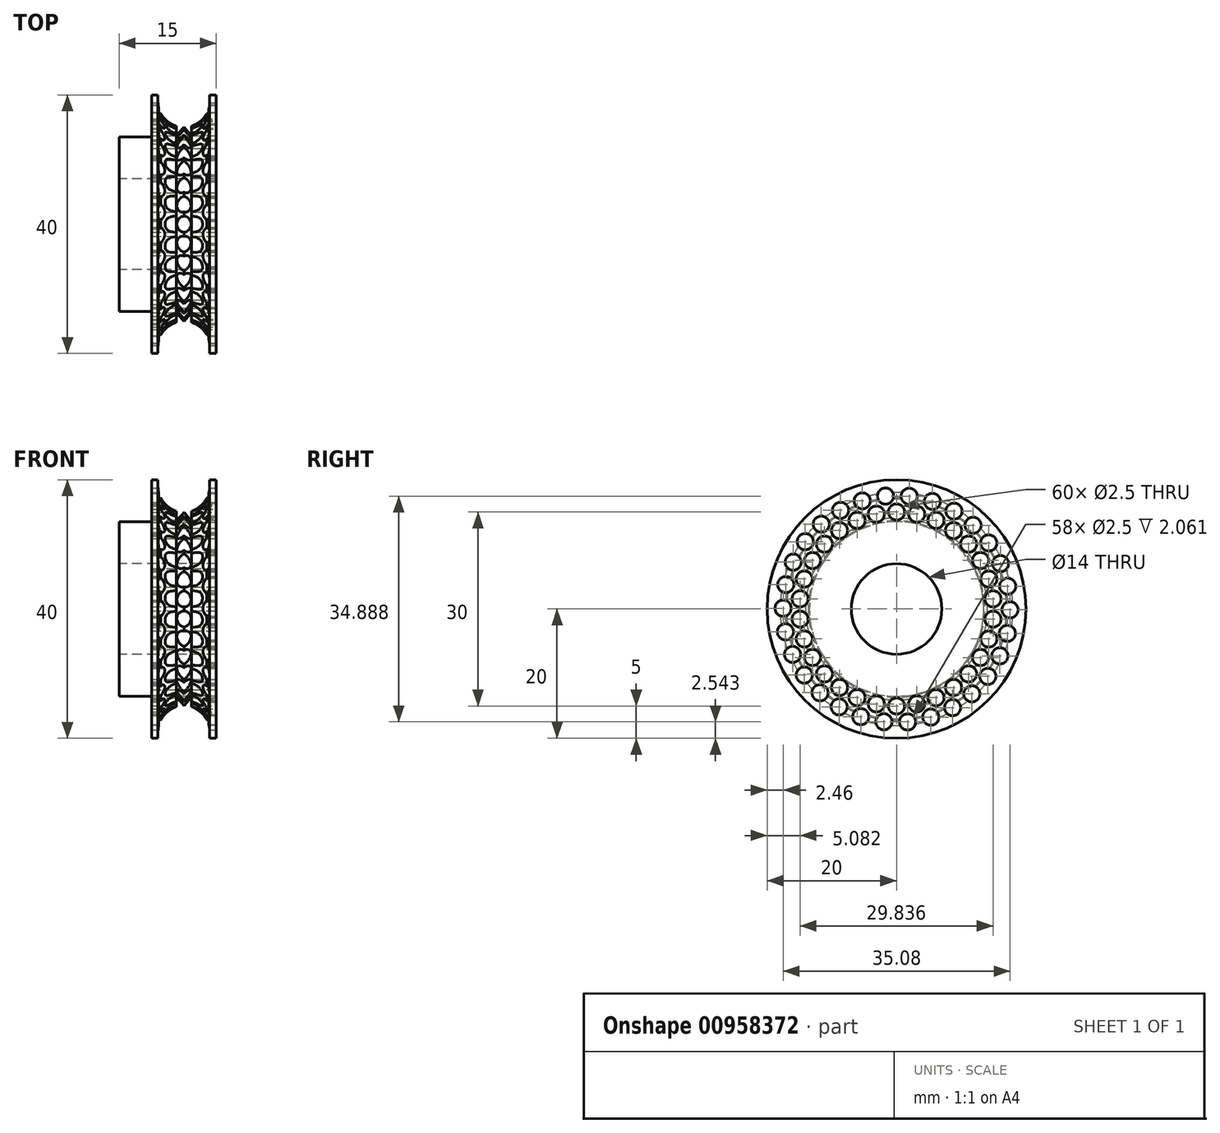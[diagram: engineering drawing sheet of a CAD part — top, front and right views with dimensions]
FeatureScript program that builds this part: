
annotation { "Feature Type Name" : "Feature", "Feature Type Description" : "" }
export const myFeature = defineFeature(function(context is Context, id is Id, definition is map)
    precondition{}
    {
        {
            var Q0;
            Q0=qCreatedBy(makeId("Top.planeOp"),FACE);
            var sketch = newSketch(context, id + "F0", { "sketchPlane" : qUnion([Q0])});
            skLineSegment(sketch, "E0", {"start": v(-12.87, 0) * mm, "end": v(26.57, 0) * mm});
            skLineSegment(sketch, "E1", {"start": v(-2.18, 7) * mm, "end": v(7.82, 7) * mm});
            skLineSegment(sketch, "E2", {"start": v(7.82, 7) * mm, "end": v(7.82, 20) * mm});
            skLineSegment(sketch, "E3", {"start": v(7.82, 20) * mm, "end": v(6.82, 20) * mm});
            skLineSegment(sketch, "E4", {"start": v(-2.18, 20) * mm, "end": v(-2.18, 7) * mm});
            skLineSegment(sketch, "E5", {"start": v(-1.18, 19) * mm, "end": v(-1.18, 20) * mm});
            skLineSegment(sketch, "E6", {"start": v(6.82, 19) * mm, "end": v(6.82, 20) * mm});
            skLineSegment(sketch, "E7.trimOffspring", {"start": v(-1.18, 20) * mm, "end": v(-2.18, 20) * mm});
            skLineSegment(sketch, "E8.direction1", {"start": v(-0.45, 12.73) * mm, "end": v(-1.73, 12.73) * mm, "construction": true});
            skLineSegment(sketch, "E9.trimOffspring", {"start": v(1.63, 15.18) * mm, "end": v(1.63, 14.05) * mm});
            skPoint(sketch, "E10.trimOffspring.end.orphan", {"position": v(-3, 12.73) * mm});
            skLineSegment(sketch, "E11.MirrorCS", {"start": v(2.84, 15) * mm, "end": v(4.02, 13.65) * mm});
            skLineSegment(sketch, "E12.MirrorCS", {"start": v(4.02, 15.18) * mm, "end": v(4.02, 13.65) * mm});
            skPoint(sketch, "E13.start.orphan", {"position": v(2.82, 15) * mm});
            skArc(sketch, "E14", {"start": v(-1.18, 19) * mm, "mid": v(-1.14, 18.5) * mm, "end": v(-1.05, 18) * mm});
            skArc(sketch, "E15", {"start": v(4.02, 15.18) * mm, "mid": v(5.4, 15.94) * mm, "end": v(6.38, 17.16) * mm});
            skLineSegment(sketch, "E16", {"start": v(2.84, 15) * mm, "end": v(1.64, 13.64) * mm});
            skLineSegment(sketch, "E17", {"start": v(1.64, 13.64) * mm, "end": v(1.63, 14.05) * mm});
            skLineSegment(sketch, "E18", {"start": v(6.7, 18) * mm, "end": v(6.7, 17) * mm});
            skLineSegment(sketch, "E19", {"start": v(6.7, 17) * mm, "end": v(6.38, 17.16) * mm});
            skArc(sketch, "E20.trimOffspring", {"start": v(6.7, 18) * mm, "mid": v(6.8, 18.5) * mm, "end": v(6.82, 19) * mm});
            skLineSegment(sketch, "E21.MirrorCS", {"start": v(-1.05, 17) * mm, "end": v(-0.73, 17.16) * mm});
            skLineSegment(sketch, "E22.MirrorCS", {"start": v(-1.05, 18) * mm, "end": v(-1.05, 17) * mm});
            skArc(sketch, "E23.trimOffspring", {"start": v(-0.73, 17.16) * mm, "mid": v(0.25, 15.94) * mm, "end": v(1.63, 15.18) * mm});
            skSolve(sketch);
        }
        {
            var Q0;
            Q0 = qSketchRegion(id + "F0", true);
            var Q1;
            Q1=sQuery(id+"F0.wireOp",EDGE,"E0");
            revolve(context, id + "F1", {"surfaceOperationType" : NewSurfaceOperationType.NEW, "entities" : qUnion([Q0]), "axis" : qUnion([Q1]), "revolveType" : RevolveType.FULL});
        }
        {
            var Q0;
            Q0=makeQuery(id+"F1.opRevolve","SWEPT_FACE",FACE,{"disambiguationData":[OSD([sQuery(id+"F0.wireOp",EDGE,"E2")])]});
            var sketch = newSketch(context, id + "F2", { "sketchPlane" : qUnion([Q0])});
            skCircle(sketch, "E24", {"center": v(0, 15) * mm, "radius": 1.25 * mm});
            skCircle(sketch, "E25.1.0", {"center": v(-8.82, 12.14) * mm, "radius": 1.25 * mm});
            skCircle(sketch, "E25.2.0", {"center": v(-14.27, 4.64) * mm, "radius": 1.25 * mm});
            skCircle(sketch, "E25.3.0", {"center": v(-14.27, -4.64) * mm, "radius": 1.25 * mm});
            skCircle(sketch, "E25.4.0", {"center": v(-8.82, -12.14) * mm, "radius": 1.25 * mm});
            skCircle(sketch, "E25.5.0", {"center": v(0, -15) * mm, "radius": 1.25 * mm});
            skCircle(sketch, "E25.6.0", {"center": v(8.82, -12.14) * mm, "radius": 1.25 * mm});
            skCircle(sketch, "E25.7.0", {"center": v(14.27, -4.64) * mm, "radius": 1.25 * mm});
            skCircle(sketch, "E25.8.0", {"center": v(14.27, 4.64) * mm, "radius": 1.25 * mm});
            skCircle(sketch, "E25.9.0", {"center": v(8.82, 12.14) * mm, "radius": 1.25 * mm});
            skPoint(sketch, "E25.center", {"position": v(0, 0) * mm});
            skCircle(sketch, "E26.1.0", {"center": v(-6.1, -13.7) * mm, "radius": 1.25 * mm});
            skCircle(sketch, "E26.1.2", {"center": v(6.1, 13.7) * mm, "radius": 1.25 * mm});
            skCircle(sketch, "E26.1.3", {"center": v(-11.15, 10.04) * mm, "radius": 1.25 * mm});
            skCircle(sketch, "E26.1.4", {"center": v(-3.12, 14.67) * mm, "radius": 1.25 * mm});
            skCircle(sketch, "E26.1.5", {"center": v(3.12, -14.67) * mm, "radius": 1.25 * mm});
            skCircle(sketch, "E26.1.6", {"center": v(11.15, -10.04) * mm, "radius": 1.25 * mm});
            skCircle(sketch, "E26.1.7", {"center": v(13, 7.5) * mm, "radius": 1.25 * mm});
            skCircle(sketch, "E26.1.8", {"center": v(-13, -7.5) * mm, "radius": 1.25 * mm});
            skCircle(sketch, "E26.1.9", {"center": v(14.92, -1.57) * mm, "radius": 1.25 * mm});
            skCircle(sketch, "E26.1.10", {"center": v(-14.92, 1.57) * mm, "radius": 1.25 * mm});
            skCircle(sketch, "E26.2.0", {"center": v(14.92, 1.57) * mm, "radius": 1.25 * mm});
            skCircle(sketch, "E26.2.2", {"center": v(-14.92, -1.57) * mm, "radius": 1.25 * mm});
            skCircle(sketch, "E26.2.3", {"center": v(-3.12, -14.67) * mm, "radius": 1.25 * mm});
            skCircle(sketch, "E26.2.4", {"center": v(-11.15, -10.04) * mm, "radius": 1.25 * mm});
            skCircle(sketch, "E26.2.5", {"center": v(11.15, 10.04) * mm, "radius": 1.25 * mm});
            skCircle(sketch, "E26.2.6", {"center": v(3.12, 14.67) * mm, "radius": 1.25 * mm});
            skCircle(sketch, "E26.2.7", {"center": v(-13, 7.5) * mm, "radius": 1.25 * mm});
            skCircle(sketch, "E26.2.8", {"center": v(13, -7.5) * mm, "radius": 1.25 * mm});
            skCircle(sketch, "E26.2.9", {"center": v(-6.1, 13.7) * mm, "radius": 1.25 * mm});
            skCircle(sketch, "E26.2.10", {"center": v(6.1, -13.7) * mm, "radius": 1.25 * mm});
            skCircle(sketch, "E27", {"center": v(1.96, 17.43) * mm, "radius": 1.25 * mm});
            skCircle(sketch, "E28.1.0", {"center": v(-8.66, 15.25) * mm, "radius": 1.25 * mm});
            skCircle(sketch, "E28.2.0", {"center": v(-15.97, 7.25) * mm, "radius": 1.25 * mm});
            skCircle(sketch, "E28.3.0", {"center": v(-17.18, -3.53) * mm, "radius": 1.25 * mm});
            skCircle(sketch, "E28.4.0", {"center": v(-11.83, -12.95) * mm, "radius": 1.25 * mm});
            skCircle(sketch, "E28.5.0", {"center": v(-1.96, -17.43) * mm, "radius": 1.25 * mm});
            skCircle(sketch, "E28.6.0", {"center": v(8.66, -15.25) * mm, "radius": 1.25 * mm});
            skCircle(sketch, "E28.7.0", {"center": v(15.97, -7.25) * mm, "radius": 1.25 * mm});
            skCircle(sketch, "E28.8.0", {"center": v(17.18, 3.53) * mm, "radius": 1.25 * mm});
            skCircle(sketch, "E28.9.0", {"center": v(11.83, 12.95) * mm, "radius": 1.25 * mm});
            skCircle(sketch, "E29.1.0", {"center": v(-11.64, 13.12) * mm, "radius": 1.25 * mm});
            skCircle(sketch, "E29.1.1", {"center": v(-17.13, 3.77) * mm, "radius": 1.25 * mm});
            skCircle(sketch, "E29.1.2", {"center": v(-16.07, -7.02) * mm, "radius": 1.25 * mm});
            skCircle(sketch, "E29.1.3", {"center": v(-8.88, -15.13) * mm, "radius": 1.25 * mm});
            skCircle(sketch, "E29.1.4", {"center": v(1.71, -17.46) * mm, "radius": 1.25 * mm});
            skCircle(sketch, "E29.1.5", {"center": v(11.64, -13.12) * mm, "radius": 1.25 * mm});
            skCircle(sketch, "E29.1.6", {"center": v(17.13, -3.77) * mm, "radius": 1.25 * mm});
            skCircle(sketch, "E29.1.7", {"center": v(16.07, 7.02) * mm, "radius": 1.25 * mm});
            skCircle(sketch, "E29.1.8", {"center": v(8.88, 15.13) * mm, "radius": 1.25 * mm});
            skCircle(sketch, "E29.1.9", {"center": v(-1.71, 17.46) * mm, "radius": 1.25 * mm});
            skCircle(sketch, "E29.2.0", {"center": v(-5.54, -16.64) * mm, "radius": 1.25 * mm});
            skCircle(sketch, "E29.2.1", {"center": v(5.3, -16.72) * mm, "radius": 1.25 * mm});
            skCircle(sketch, "E29.2.2", {"center": v(14.12, -10.4) * mm, "radius": 1.25 * mm});
            skCircle(sketch, "E29.2.3", {"center": v(17.54, -0.12) * mm, "radius": 1.25 * mm});
            skCircle(sketch, "E29.2.4", {"center": v(14.26, 10.2) * mm, "radius": 1.25 * mm});
            skCircle(sketch, "E29.2.5", {"center": v(5.54, 16.64) * mm, "radius": 1.25 * mm});
            skCircle(sketch, "E29.2.6", {"center": v(-5.3, 16.72) * mm, "radius": 1.25 * mm});
            skCircle(sketch, "E29.2.7", {"center": v(-14.12, 10.4) * mm, "radius": 1.25 * mm});
            skCircle(sketch, "E29.2.8", {"center": v(-17.54, 0.12) * mm, "radius": 1.25 * mm});
            skCircle(sketch, "E29.2.9", {"center": v(-14.26, -10.2) * mm, "radius": 1.25 * mm});
            skSolve(sketch);
        }
        {
            var Q0;
            Q0 = qSketchRegion(id + "F2", true);
            extrude(context, id + "F3", {"entities" : qUnion([Q0]), "operationType" : NewBodyOperationType.REMOVE, "oppositeDirection" : true, "depth" : 25 * mm, "offsetDistance" : 25 * mm});
        }
        {
            var Q0;
            Q0=makeQuery(id+"F1.opRevolve","SWEPT_FACE",FACE,{"disambiguationData":[OSD([sQuery(id+"F0.wireOp",EDGE,"E4")])]});
            var sketch = newSketch(context, id + "F4", { "sketchPlane" : qUnion([Q0])});
            skCircle(sketch, "E30", {"center": v(0, 0) * mm, "radius": 13.5 * mm});
            skCircle(sketch, "E31", {"center": v(0, 0) * mm, "radius": 7 * mm});
            skSolve(sketch);
        }
        {
            var Q0;
            Q0 = qSketchRegion(id + "F4", true);
            extrude(context, id + "F5", {"entities" : qUnion([Q0]), "operationType" : NewBodyOperationType.ADD, "depth" : 5 * mm, "offsetDistance" : 25 * mm});
        }
    });
